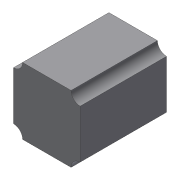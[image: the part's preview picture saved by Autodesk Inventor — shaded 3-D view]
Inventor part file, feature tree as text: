
AUTODESK INVENTOR PART (.ipt)
format: ipt  version: 2018 (Build 220112000, 112)  size: 109,568 bytes
history: native  units: mm
features: extrude x3, sketch x3, projected_geometry x1
ambient origin geometry x8: Origin, YZ Plane, XZ Plane, XY Plane, X Axis, Y Axis, Z Axis, Center Point
bodies: Solid1 (feature_tree)
feature tree (7):
  extrude  "Extrusion1"  Depth=22.0mm
  extrude  "Extrusion2"  Depth=28.5mm
  extrude  "Extrusion3"  Depth=10.0mm
  sketch  "Sketch1"  dims[d0=22.0mm d1=22.0mm]
  sketch  "Sketch2"  dims[d2=28.5mm d3=0.0mm d4=18.0mm]
  sketch  "Sketch3"  dims[d5=14.5mm d6=0.0mm d7=6.0mm d8=6.0mm d9=6.0mm d10=6.0mm d11=10.0mm d12=0.0mm]
  projected_geometry  "Projected Loop1"
